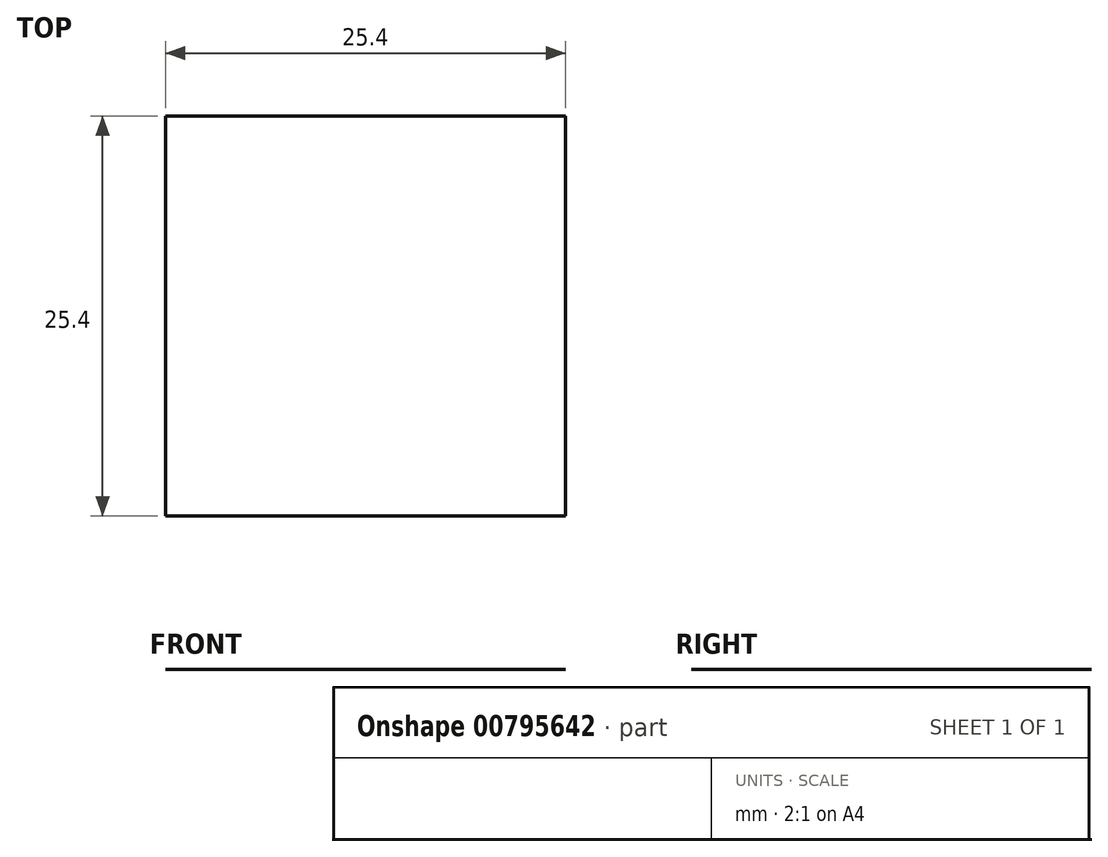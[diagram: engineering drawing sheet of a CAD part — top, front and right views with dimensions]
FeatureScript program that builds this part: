
annotation { "Feature Type Name" : "Feature", "Feature Type Description" : "" }
export const myFeature = defineFeature(function(context is Context, id is Id, definition is map)
    precondition{}
    {
        {
            var Q0;
            Q0=qCreatedBy(makeId("Front.planeOp"),FACE);
            var sketch = newSketch(context, id + "F0", { "sketchPlane" : qUnion([Q0])});
            skLineSegment(sketch, "E0", {"start": v(0, 0) * mm, "end": v(25.4, 0) * mm});
            skSolve(sketch);
        }
        {
            var Q0;
            Q0=sQuery(id+"F0.wireOp",EDGE,"E0");
            extrude(context, id + "F1", {"bodyType" : ToolBodyType.SURFACE, "surfaceEntities" : qUnion([Q0]), "depth" : 25.4 * mm, "offsetDistance" : 25.4 * mm});
        }
    });
